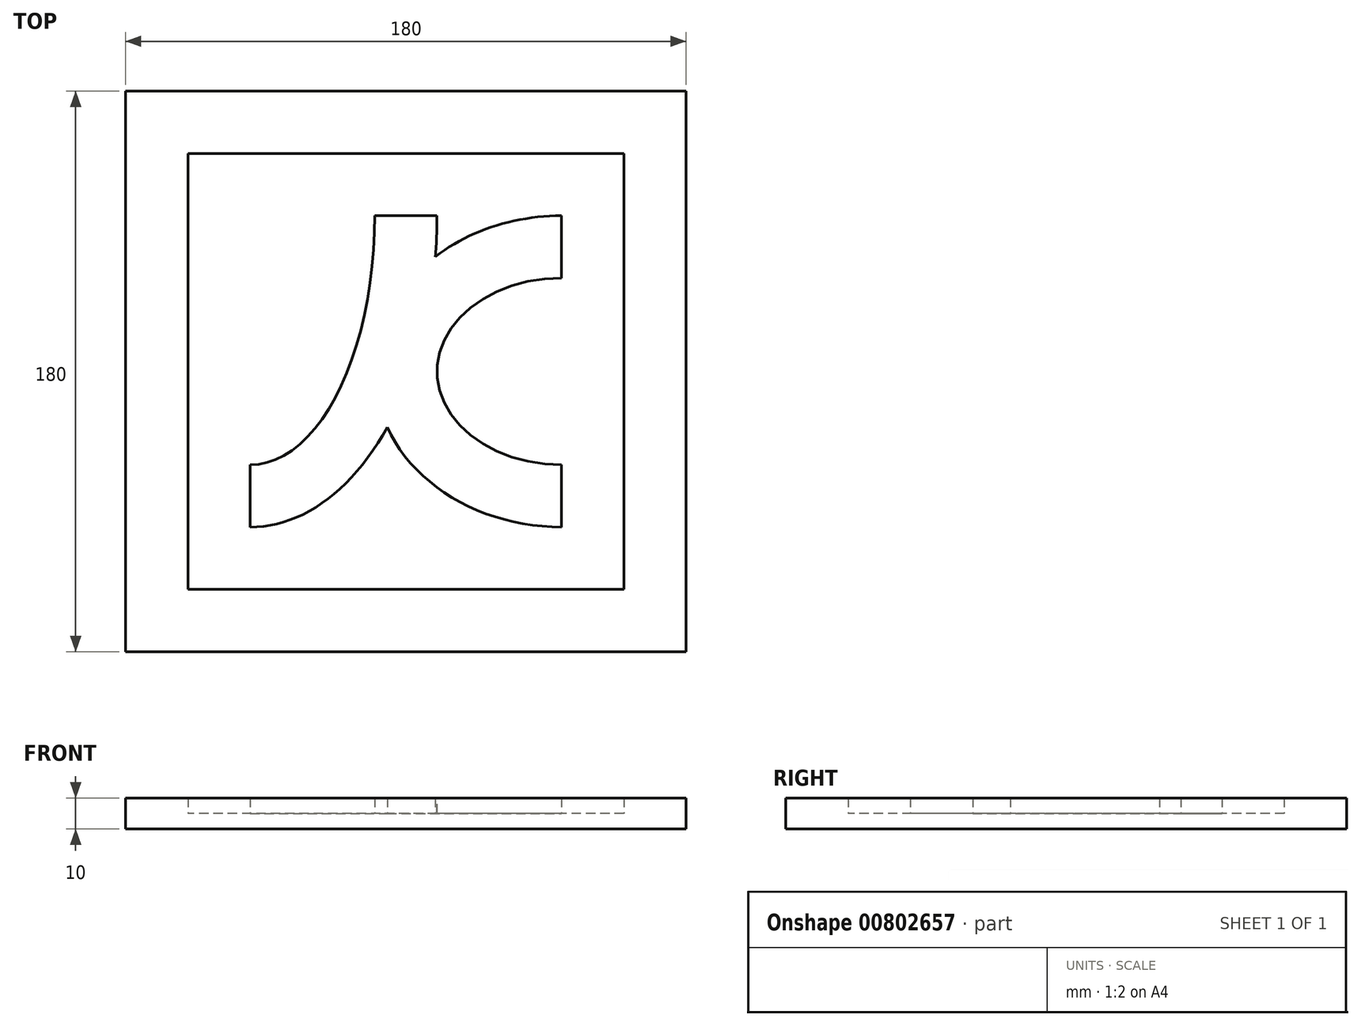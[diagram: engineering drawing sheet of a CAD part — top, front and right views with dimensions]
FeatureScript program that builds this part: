
annotation { "Feature Type Name" : "Feature", "Feature Type Description" : "" }
export const myFeature = defineFeature(function(context is Context, id is Id, definition is map)
    precondition{}
    {
        {
            var Q0;
            Q0=qCreatedBy(makeId("Top.planeOp"),FACE);
            var sketch = newSketch(context, id + "F0", { "sketchPlane" : qUnion([Q0])});
            skLineSegment(sketch, "E0.bottom", {"start": v(90, 90) * mm, "end": v(-90, 90) * mm});
            skLineSegment(sketch, "E0.top", {"start": v(90, -90) * mm, "end": v(-90, -90) * mm});
            skLineSegment(sketch, "E0.left", {"start": v(90, 90) * mm, "end": v(90, -90) * mm});
            skLineSegment(sketch, "E0.right", {"start": v(-90, 90) * mm, "end": v(-90, -90) * mm});
            skPoint(sketch, "E0.middle", {"position": v(0, 0) * mm});
            skSolve(sketch);
        }
        {
            var Q0;
            Q0=makeQuery(id+"F0.imprint","IMPRINT",FACE,{"disambiguationData":[TD([[makeQuery(id+"F0.imprint","IMPRINT",EDGE,{"derivedFrom":sQuery(id+"F0.wireOp",EDGE,"E0.bottom")}),1.0]])]});
            extrude(context, id + "F1", {"entities" : qUnion([Q0]), "depth" : 5 * mm, "offsetDistance" : 25 * mm});
        }
        {
            var Q0;
            Q0=makeQuery(id+"F1.opExtrude","CAP_FACE",FACE,{"disambiguationData":[OSD([sQuery(id+"F0.wireOp",EDGE,"E0.bottom"),sQuery(id+"F0.wireOp",EDGE,"E0.top"),sQuery(id+"F0.wireOp",EDGE,"E0.left"),sQuery(id+"F0.wireOp",EDGE,"E0.right")])],"isStart":false});
            var sketch = newSketch(context, id + "F2", { "sketchPlane" : qUnion([Q0])});
            skLineSegment(sketch, "E1.bottom", {"start": v(90, 90) * mm, "end": v(-90, 90) * mm});
            skLineSegment(sketch, "E1.top", {"start": v(90, -90) * mm, "end": v(-90, -90) * mm});
            skLineSegment(sketch, "E1.left", {"start": v(90, 90) * mm, "end": v(90, -90) * mm});
            skLineSegment(sketch, "E1.right", {"start": v(-90, 90) * mm, "end": v(-90, -90) * mm});
            skPoint(sketch, "E1.middle", {"position": v(0, 0) * mm});
            skLineSegment(sketch, "E2.bottom", {"start": v(70, 70) * mm, "end": v(-70, 70) * mm});
            skLineSegment(sketch, "E2.top", {"start": v(70, -70) * mm, "end": v(-70, -70) * mm});
            skLineSegment(sketch, "E2.left", {"start": v(70, 70) * mm, "end": v(70, -70) * mm});
            skLineSegment(sketch, "E2.right", {"start": v(-70, 70) * mm, "end": v(-70, -70) * mm});
            skLineSegment(sketch, "E3.bottom", {"start": v(50, 50) * mm, "end": v(-50, 50) * mm});
            skLineSegment(sketch, "E3.top", {"start": v(50, -50) * mm, "end": v(-50, -50) * mm});
            skLineSegment(sketch, "E3.left", {"start": v(50, 50) * mm, "end": v(50, -50) * mm});
            skLineSegment(sketch, "E3.right", {"start": v(-50, 50) * mm, "end": v(-50, -50) * mm});
            skEllipse(sketch, "E4", {"center": v(-50, 50) * mm, "majorRadius": 100 * mm, "minorRadius": 60 * mm, "majorAxis": v(0, 1)});
            skEllipse(sketch, "E5", {"center": v(-50, 50) * mm, "majorRadius": 80 * mm, "minorRadius": 40 * mm, "majorAxis": v(0, -1)});
            skLineSegment(sketch, "E6.bottom", {"start": v(-50, 50) * mm, "end": v(0, 50) * mm});
            skLineSegment(sketch, "E6.top", {"start": v(-50, 30) * mm, "end": v(0, 30) * mm});
            skLineSegment(sketch, "E6.left", {"start": v(-50, 50) * mm, "end": v(-50, 30) * mm});
            skLineSegment(sketch, "E6.right", {"start": v(0, 50) * mm, "end": v(0, 30) * mm});
            skEllipse(sketch, "E7", {"center": v(50, 0) * mm, "majorRadius": 50 * mm, "minorRadius": 60 * mm, "majorAxis": v(0, 1)});
            skEllipse(sketch, "E8", {"center": v(50, 0) * mm, "majorRadius": 40 * mm, "minorRadius": 30 * mm, "majorAxis": v(-1, 0)});
            skSolve(sketch);
        }
        {
            var Q0;
            {var subQ0=sQuery(id+"F2.wireOp",EDGE,"E1.right");var subQ1=sQuery(id+"F2.wireOp",EDGE,"E1.bottom");var subQ2=makeQuery(id+"F2.imprint","INTERSECT",VERTEX,{"derivedFrom":[subQ1,subQ0]});Q0=makeQuery(id+"F2.imprint","IMPRINT",FACE,{"disambiguationData":[TD([[makeQuery(id+"F2.imprint","IMPRINT",EDGE,{"disambiguationData":[TD([[subQ2,1.0]])],"derivedFrom":subQ1}),1.0]])]});}
            var Q1;
            {var subQ0=sQuery(id+"F2.wireOp",EDGE,"E5");var subQ1=sQuery(id+"F2.wireOp",EDGE,"E1.bottom");var subQ2=makeQuery(id+"F2.imprint","INTERSECT",VERTEX,{"disambiguationData":[OD(0.0)],"derivedFrom":[subQ1,subQ0]});Q1=makeQuery(id+"F2.imprint","IMPRINT",FACE,{"disambiguationData":[TD([[makeQuery(id+"F2.imprint","IMPRINT",EDGE,{"disambiguationData":[TD([[subQ2,-1.0]])],"derivedFrom":subQ1}),1.0]])]});}
            var Q2;
            {var subQ0=sQuery(id+"F2.wireOp",EDGE,"E4");var subQ1=sQuery(id+"F2.wireOp",EDGE,"E1.bottom");var subQ2=makeQuery(id+"F2.imprint","INTERSECT",VERTEX,{"derivedFrom":[subQ1,subQ0]});Q2=makeQuery(id+"F2.imprint","IMPRINT",FACE,{"disambiguationData":[TD([[makeQuery(id+"F2.imprint","IMPRINT",EDGE,{"disambiguationData":[TD([[subQ2,-1.0]])],"derivedFrom":subQ1}),1.0]])]});}
            var Q3;
            {var subQ5=sQuery(id+"F2.wireOp",EDGE,"E1.left");var subQ6=sQuery(id+"F2.wireOp",EDGE,"E1.bottom");var subQ7=makeQuery(id+"F2.imprint","INTERSECT",VERTEX,{"derivedFrom":[subQ6,subQ5]});Q3=makeQuery(id+"F2.imprint","IMPRINT",FACE,{"disambiguationData":[TD([[makeQuery(id+"F2.imprint","IMPRINT",EDGE,{"disambiguationData":[TD([[subQ7,-1.0]])],"derivedFrom":subQ6}),1.0]])]});}
            var Q4;
            {var subQ0=sQuery(id+"F2.wireOp",EDGE,"E7");var subQ1=sQuery(id+"F2.wireOp",EDGE,"E1.left");var subQ2=makeQuery(id+"F2.imprint","INTERSECT",VERTEX,{"disambiguationData":[OD(0.0)],"derivedFrom":[subQ1,subQ0]});Q4=makeQuery(id+"F2.imprint","IMPRINT",FACE,{"disambiguationData":[TD([[makeQuery(id+"F2.imprint","IMPRINT",EDGE,{"disambiguationData":[TD([[subQ2,-1.0]])],"derivedFrom":subQ1}),-1.0]])]});}
            var Q5;
            {var subQ0=sQuery(id+"F2.wireOp",EDGE,"E8");var subQ1=sQuery(id+"F2.wireOp",EDGE,"E2.left");var subQ2=makeQuery(id+"F2.imprint","INTERSECT",VERTEX,{"disambiguationData":[OD(0.0)],"derivedFrom":[subQ1,subQ0]});Q5=makeQuery(id+"F2.imprint","IMPRINT",FACE,{"disambiguationData":[TD([[makeQuery(id+"F2.imprint","IMPRINT",EDGE,{"disambiguationData":[TD([[subQ2,-1.0]])],"derivedFrom":subQ1}),1.0]])]});}
            var Q6;
            {var subQ0=sQuery(id+"F2.wireOp",EDGE,"E7");var subQ1=sQuery(id+"F2.wireOp",EDGE,"E1.left");var subQ2=makeQuery(id+"F2.imprint","INTERSECT",VERTEX,{"disambiguationData":[OD(1.0)],"derivedFrom":[subQ1,subQ0]});Q6=makeQuery(id+"F2.imprint","IMPRINT",FACE,{"disambiguationData":[TD([[makeQuery(id+"F2.imprint","IMPRINT",EDGE,{"disambiguationData":[TD([[subQ2,1.0]])],"derivedFrom":subQ1}),-1.0]])]});}
            var Q7;
            {var subQ0=sQuery(id+"F2.wireOp",EDGE,"E4");var subQ1=sQuery(id+"F2.wireOp",EDGE,"E1.right");var subQ2=makeQuery(id+"F2.imprint","INTERSECT",VERTEX,{"derivedFrom":[subQ1,subQ0]});Q7=makeQuery(id+"F2.imprint","IMPRINT",FACE,{"disambiguationData":[TD([[makeQuery(id+"F2.imprint","IMPRINT",EDGE,{"disambiguationData":[TD([[subQ2,1.0]])],"derivedFrom":subQ1}),1.0]])]});}
            var Q8;
            {var subQ8=sQuery(id+"F2.wireOp",EDGE,"E6.right");Q8=makeQuery(id+"F2.imprint","IMPRINT",FACE,{"disambiguationData":[TD([[makeQuery(id+"F2.imprint","IMPRINT",EDGE,{"derivedFrom":subQ8}),1.0]])]});}
            var Q9;
            {var subQ5=sQuery(id+"F2.wireOp",EDGE,"E6.right");Q9=makeQuery(id+"F2.imprint","IMPRINT",FACE,{"disambiguationData":[TD([[makeQuery(id+"F2.imprint","IMPRINT",EDGE,{"derivedFrom":subQ5}),-1.0]])]});}
            var Q10;
            {var subQ5=sQuery(id+"F2.wireOp",EDGE,"E6.left");Q10=makeQuery(id+"F2.imprint","IMPRINT",FACE,{"disambiguationData":[TD([[makeQuery(id+"F2.imprint","IMPRINT",EDGE,{"derivedFrom":subQ5}),1.0]])]});}
            var Q11;
            {var subQ0=sQuery(id+"F2.wireOp",EDGE,"E7");var subQ1=sQuery(id+"F2.wireOp",EDGE,"E4");var subQ2=makeQuery(id+"F2.imprint","INTERSECT",VERTEX,{"disambiguationData":[OD(0.0)],"derivedFrom":[subQ1,subQ0]});Q11=makeQuery(id+"F2.imprint","IMPRINT",FACE,{"disambiguationData":[TD([[makeQuery(id+"F2.imprint","IMPRINT",EDGE,{"disambiguationData":[TD([[subQ2,-1.0]])],"derivedFrom":subQ1}),-1.0]])]});}
            var Q12;
            {var subQ0=sQuery(id+"F2.wireOp",EDGE,"E7");var subQ1=sQuery(id+"F2.wireOp",EDGE,"E4");var subQ2=makeQuery(id+"F2.imprint","INTERSECT",VERTEX,{"disambiguationData":[OD(0.0)],"derivedFrom":[subQ1,subQ0]});Q12=makeQuery(id+"F2.imprint","IMPRINT",FACE,{"disambiguationData":[TD([[makeQuery(id+"F2.imprint","IMPRINT",EDGE,{"disambiguationData":[TD([[subQ2,-1.0]])],"derivedFrom":subQ1}),1.0]])]});}
            var Q13;
            {var subQ1=sQuery(id+"F2.wireOp",EDGE,"E1.top");Q13=makeQuery(id+"F2.imprint","IMPRINT",FACE,{"disambiguationData":[TD([[makeQuery(id+"F2.imprint","IMPRINT",EDGE,{"derivedFrom":subQ1}),-1.0]])]});}
            extrude(context, id + "F3", {"entities" : qUnion([Q0, Q1, Q2, Q3, Q4, Q5, Q6, Q7, Q8, Q9, Q10, Q11, Q12, Q13]), "operationType" : NewBodyOperationType.ADD, "depth" : 5 * mm, "offsetDistance" : 25 * mm});
        }
    });
